# Revit family: NAGARE_STRAIGHT-50
name_source: partatom
category: Site
units: mm (PartAtom-declared; Revit-internal decimal feet)

## family parameters
Always vertical = Yes
Cut with Voids When Loaded = No
Part Type = Normal
Round Connector Dimension = Use Diameter
Shared = Yes
Work Plane-Based = Yes

## types (9) — shared parameters
Manufacturer = www.nagareconcrete.com
URL = https://www.nagareconcrete.com
materiaal_model = NAGARE_FME_(9-).f2_BETON_SI_BERSnl
model_breedte = 500 mm  [stored 1.64042 ft]
offset_10 = 10 mm  [stored 0.0328084 ft]
zero-valued in all types: Default Elevation

## per-type parameters (varying)
| type | beugelpositie_hoogte | model_hoogte | oksel_maatvoering_breedte | oksel_maatvoering_hoogte | voet_hoogte | voet_lengte | voet_type2_150 | voet_type2_base-breedte | voet_type2_hoogte |
| LP100/50 | 500 mm  [stored 1.64042 ft] | 1000 mm | 60 mm  [stored 0.19685 ft] | 60 mm  [stored 0.19685 ft] | 120 mm | 600 mm | No | 30 mm  [stored 0.0984252 ft] | 600 mm |
| LP125/50 | 625 mm | 1250 mm | 90 mm | 90 mm | 120 mm | 750 mm  [stored 2.46063 ft] | No | 30 mm  [stored 0.0984252 ft] | 600 mm |
| LP150/50 | 750 mm  [stored 2.46063 ft] | 1500 mm | 90 mm | 90 mm | 120 mm | 850 mm | No | 30 mm  [stored 0.0984252 ft] | 600 mm |
| LP175/50 | 875 mm | 1750 mm | 125 mm | 125 mm | 120 mm | 1100 mm | No | 30 mm  [stored 0.0984252 ft] | 600 mm |
| LP200/50 | 1000 mm | 2000 mm  [stored 6.56168 ft] | 125 mm | 125 mm | 120 mm | 1100 mm | No | 30 mm  [stored 0.0984252 ft] | 600 mm |
| LP225/50 | 1125 mm | 2250 mm | 280 mm | 280 mm | 150 mm | 1350 mm | Yes | 30 mm  [stored 0.0984252 ft] | 600 mm |
| LP250/50 | 1250 mm | 2500 mm | 280 mm | 310 mm | 150 mm | 1350 mm | Yes | 55 mm | 800 mm |
| LP75/50 | 375 mm | 750 mm  [stored 2.46063 ft] | 20 mm  [stored 0.0656168 ft] | 20 mm  [stored 0.0656168 ft] | 120 mm | 500 mm  [stored 1.64042 ft] | No | 30 mm  [stored 0.0984252 ft] | 600 mm |
| LP50/50 | 275 mm | 500 mm  [stored 1.64042 ft] | 20 mm  [stored 0.0656168 ft] | 20 mm  [stored 0.0656168 ft] | 120 mm | 400 mm  [stored 1.31234 ft] | No | 30 mm  [stored 0.0984252 ft] | 600 mm |

note: column(s) folded — value = type name in every type: Type Comments

note: [stored X ft] marks values corroborated as IEEE doubles in the binary element streams (Revit-internal decimal feet)

## geometry (parser evidence)
native form markers: Sweep x2
no freeform markers — native parametric forms only
